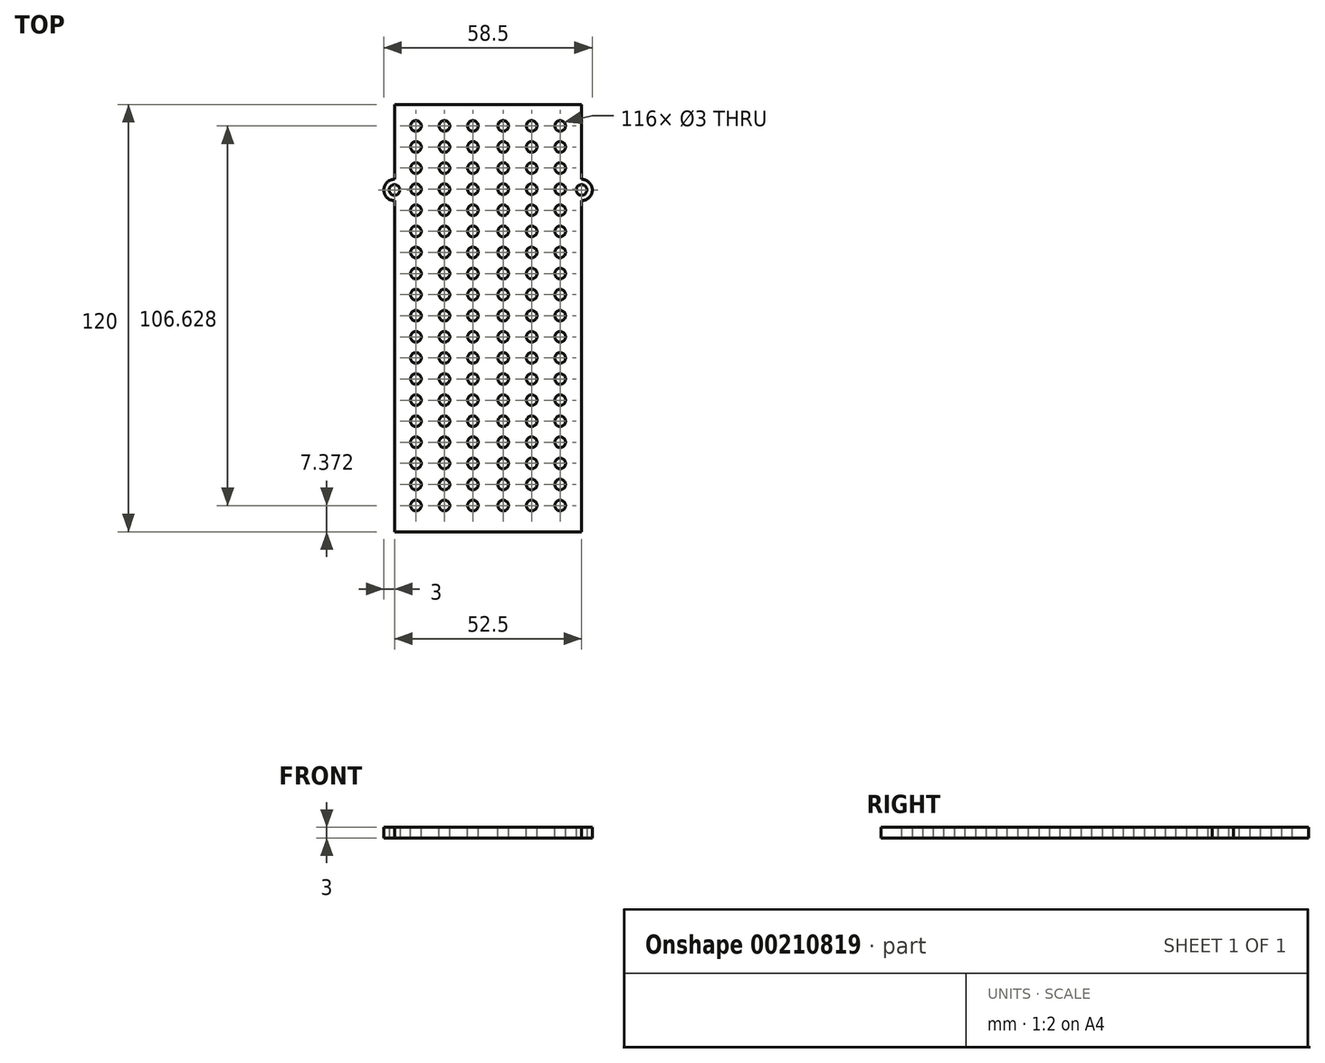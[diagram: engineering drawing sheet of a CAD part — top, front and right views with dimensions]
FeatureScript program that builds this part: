
annotation { "Feature Type Name" : "Feature", "Feature Type Description" : "" }
export const myFeature = defineFeature(function(context is Context, id is Id, definition is map)
    precondition{}
    {
        {
            var Q0;
            Q0=qCreatedBy(makeId("Top.planeOp"),FACE);
            var sketch = newSketch(context, id + "F0", { "sketchPlane" : qUnion([Q0])});
            skCircle(sketch, "E0", {"center": v(-26.25, 36) * mm, "radius": 1.5 * mm});
            skCircle(sketch, "E1", {"center": v(26.25, 36) * mm, "radius": 1.5 * mm});
            skLineSegment(sketch, "E2.bottom", {"start": v(-26.25, 60) * mm, "end": v(26.25, 60) * mm});
            skLineSegment(sketch, "E2.top", {"start": v(-26.25, -60) * mm, "end": v(26.25, -60) * mm});
            skLineSegment(sketch, "E2.left", {"start": v(-26.25, 60) * mm, "end": v(-26.25, 39) * mm});
            skPoint(sketch, "E2.middle", {"position": v(0, 0) * mm});
            skLineSegment(sketch, "E3", {"start": v(26.25, -60) * mm, "end": v(26.25, 33) * mm});
            skArc(sketch, "E4", {"start": v(-26.25, 39) * mm, "mid": v(-29.25, 36) * mm, "end": v(-26.25, 33) * mm});
            skArc(sketch, "E5", {"start": v(26.25, 33) * mm, "mid": v(29.25, 36) * mm, "end": v(26.25, 39) * mm});
            skLineSegment(sketch, "E6.trimOffspring", {"start": v(-26.25, 33) * mm, "end": v(-26.25, -60) * mm});
            skLineSegment(sketch, "E7.trimOffspring", {"start": v(26.25, 39) * mm, "end": v(26.25, 60) * mm});
            skSolve(sketch);
        }
        {
            var Q0;
            Q0 = qSketchRegion(id + "F0", true);
            extrude(context, id + "F1", {"entities" : qUnion([Q0]), "depth" : 3 * mm});
        }
        {
            var Q0;
            Q0=makeQuery(id+"F1.opExtrude","CAP_FACE",FACE,{"disambiguationData":[OSD([sQuery(id+"F0.wireOp",EDGE,"E0"),sQuery(id+"F0.wireOp",EDGE,"E1"),sQuery(id+"F0.wireOp",EDGE,"E2.bottom"),sQuery(id+"F0.wireOp",EDGE,"E2.top"),sQuery(id+"F0.wireOp",EDGE,"E2.left"),sQuery(id+"F0.wireOp",EDGE,"E3"),sQuery(id+"F0.wireOp",EDGE,"E4"),sQuery(id+"F0.wireOp",EDGE,"E5"),sQuery(id+"F0.wireOp",EDGE,"E6.trimOffspring"),sQuery(id+"F0.wireOp",EDGE,"E7.trimOffspring")])],"isStart":false});
            var sketch = newSketch(context, id + "F2", { "sketchPlane" : qUnion([Q0])});
            skLineSegment(sketch, "E8", {"start": v(-26.25, 54) * mm, "end": v(26.25, 54) * mm, "construction": true});
            skCircle(sketch, "E9", {"center": v(-20.25, 54) * mm, "radius": 1.5 * mm});
            skCircle(sketch, "E10", {"center": v(20.25, 54) * mm, "radius": 1.5 * mm});
            skCircle(sketch, "E11", {"center": v(-12.25, 54) * mm, "radius": 1.5 * mm});
            skCircle(sketch, "E12", {"center": v(12.25, 54) * mm, "radius": 1.5 * mm});
            skCircle(sketch, "E13", {"center": v(-4.25, 54) * mm, "radius": 1.5 * mm});
            skCircle(sketch, "E14", {"center": v(4.25, 54) * mm, "radius": 1.5 * mm});
            skLineSegment(sketch, "E15.direction1", {"start": v(-20.25, 54) * mm, "end": v(-20.25, 48.08) * mm, "construction": true});
            skCircle(sketch, "E16.0.1.0", {"center": v(-20.25, 48.08) * mm, "radius": 1.5 * mm});
            skCircle(sketch, "E16.2.1.0", {"center": v(-12.25, 48.08) * mm, "radius": 1.5 * mm});
            skCircle(sketch, "E16.4.1.0", {"center": v(-4.25, 48.08) * mm, "radius": 1.5 * mm});
            skCircle(sketch, "E16.6.1.0", {"center": v(4.25, 48.08) * mm, "radius": 1.5 * mm});
            skCircle(sketch, "E16.8.1.0", {"center": v(12.25, 48.08) * mm, "radius": 1.5 * mm});
            skCircle(sketch, "E16.10.1.0", {"center": v(20.25, 48.08) * mm, "radius": 1.5 * mm});
            skCircle(sketch, "E16.0.2.0", {"center": v(-20.25, 42.15) * mm, "radius": 1.5 * mm});
            skCircle(sketch, "E16.2.2.0", {"center": v(-12.25, 42.15) * mm, "radius": 1.5 * mm});
            skCircle(sketch, "E16.4.2.0", {"center": v(-4.25, 42.15) * mm, "radius": 1.5 * mm});
            skCircle(sketch, "E16.6.2.0", {"center": v(4.25, 42.15) * mm, "radius": 1.5 * mm});
            skCircle(sketch, "E16.8.2.0", {"center": v(12.25, 42.15) * mm, "radius": 1.5 * mm});
            skCircle(sketch, "E16.10.2.0", {"center": v(20.25, 42.15) * mm, "radius": 1.5 * mm});
            skCircle(sketch, "E16.0.3.0", {"center": v(-20.25, 36.23) * mm, "radius": 1.5 * mm});
            skCircle(sketch, "E16.2.3.0", {"center": v(-12.25, 36.23) * mm, "radius": 1.5 * mm});
            skCircle(sketch, "E16.4.3.0", {"center": v(-4.25, 36.23) * mm, "radius": 1.5 * mm});
            skCircle(sketch, "E16.6.3.0", {"center": v(4.25, 36.23) * mm, "radius": 1.5 * mm});
            skCircle(sketch, "E16.8.3.0", {"center": v(12.25, 36.23) * mm, "radius": 1.5 * mm});
            skCircle(sketch, "E16.10.3.0", {"center": v(20.25, 36.23) * mm, "radius": 1.5 * mm});
            skCircle(sketch, "E16.0.4.0", {"center": v(-20.25, 30.3) * mm, "radius": 1.5 * mm});
            skCircle(sketch, "E16.2.4.0", {"center": v(-12.25, 30.3) * mm, "radius": 1.5 * mm});
            skCircle(sketch, "E16.4.4.0", {"center": v(-4.25, 30.3) * mm, "radius": 1.5 * mm});
            skCircle(sketch, "E16.6.4.0", {"center": v(4.25, 30.3) * mm, "radius": 1.5 * mm});
            skCircle(sketch, "E16.8.4.0", {"center": v(12.25, 30.3) * mm, "radius": 1.5 * mm});
            skCircle(sketch, "E16.10.4.0", {"center": v(20.25, 30.3) * mm, "radius": 1.5 * mm});
            skCircle(sketch, "E16.0.5.0", {"center": v(-20.25, 24.38) * mm, "radius": 1.5 * mm});
            skCircle(sketch, "E16.2.5.0", {"center": v(-12.25, 24.38) * mm, "radius": 1.5 * mm});
            skCircle(sketch, "E16.4.5.0", {"center": v(-4.25, 24.38) * mm, "radius": 1.5 * mm});
            skCircle(sketch, "E16.6.5.0", {"center": v(4.25, 24.38) * mm, "radius": 1.5 * mm});
            skCircle(sketch, "E16.8.5.0", {"center": v(12.25, 24.38) * mm, "radius": 1.5 * mm});
            skCircle(sketch, "E16.10.5.0", {"center": v(20.25, 24.38) * mm, "radius": 1.5 * mm});
            skCircle(sketch, "E16.0.6.0", {"center": v(-20.25, 18.46) * mm, "radius": 1.5 * mm});
            skCircle(sketch, "E16.2.6.0", {"center": v(-12.25, 18.46) * mm, "radius": 1.5 * mm});
            skCircle(sketch, "E16.4.6.0", {"center": v(-4.25, 18.46) * mm, "radius": 1.5 * mm});
            skCircle(sketch, "E16.6.6.0", {"center": v(4.25, 18.46) * mm, "radius": 1.5 * mm});
            skCircle(sketch, "E16.8.6.0", {"center": v(12.25, 18.46) * mm, "radius": 1.5 * mm});
            skCircle(sketch, "E16.10.6.0", {"center": v(20.25, 18.46) * mm, "radius": 1.5 * mm});
            skCircle(sketch, "E16.0.7.0", {"center": v(-20.25, 12.53) * mm, "radius": 1.5 * mm});
            skCircle(sketch, "E16.2.7.0", {"center": v(-12.25, 12.53) * mm, "radius": 1.5 * mm});
            skCircle(sketch, "E16.4.7.0", {"center": v(-4.25, 12.53) * mm, "radius": 1.5 * mm});
            skCircle(sketch, "E16.6.7.0", {"center": v(4.25, 12.53) * mm, "radius": 1.5 * mm});
            skCircle(sketch, "E16.8.7.0", {"center": v(12.25, 12.53) * mm, "radius": 1.5 * mm});
            skCircle(sketch, "E16.10.7.0", {"center": v(20.25, 12.53) * mm, "radius": 1.5 * mm});
            skCircle(sketch, "E16.0.8.0", {"center": v(-20.25, 6.6) * mm, "radius": 1.5 * mm});
            skCircle(sketch, "E16.2.8.0", {"center": v(-12.25, 6.6) * mm, "radius": 1.5 * mm});
            skCircle(sketch, "E16.4.8.0", {"center": v(-4.25, 6.6) * mm, "radius": 1.5 * mm});
            skCircle(sketch, "E16.6.8.0", {"center": v(4.25, 6.6) * mm, "radius": 1.5 * mm});
            skCircle(sketch, "E16.8.8.0", {"center": v(12.25, 6.6) * mm, "radius": 1.5 * mm});
            skCircle(sketch, "E16.10.8.0", {"center": v(20.25, 6.6) * mm, "radius": 1.5 * mm});
            skCircle(sketch, "E16.0.9.0", {"center": v(-20.25, 0.69) * mm, "radius": 1.5 * mm});
            skCircle(sketch, "E16.2.9.0", {"center": v(-12.25, 0.69) * mm, "radius": 1.5 * mm});
            skCircle(sketch, "E16.4.9.0", {"center": v(-4.25, 0.69) * mm, "radius": 1.5 * mm});
            skCircle(sketch, "E16.6.9.0", {"center": v(4.25, 0.69) * mm, "radius": 1.5 * mm});
            skCircle(sketch, "E16.8.9.0", {"center": v(12.25, 0.69) * mm, "radius": 1.5 * mm});
            skCircle(sketch, "E16.10.9.0", {"center": v(20.25, 0.69) * mm, "radius": 1.5 * mm});
            skCircle(sketch, "E17.0.10.0", {"center": v(-20.25, -5.24) * mm, "radius": 1.5 * mm});
            skCircle(sketch, "E17.2.10.0", {"center": v(-12.25, -5.24) * mm, "radius": 1.5 * mm});
            skCircle(sketch, "E17.4.10.0", {"center": v(-4.25, -5.24) * mm, "radius": 1.5 * mm});
            skCircle(sketch, "E17.6.10.0", {"center": v(4.25, -5.24) * mm, "radius": 1.5 * mm});
            skCircle(sketch, "E17.8.10.0", {"center": v(12.25, -5.24) * mm, "radius": 1.5 * mm});
            skCircle(sketch, "E17.10.10.0", {"center": v(20.25, -5.24) * mm, "radius": 1.5 * mm});
            skCircle(sketch, "E17.0.11.0", {"center": v(-20.25, -11.16) * mm, "radius": 1.5 * mm});
            skCircle(sketch, "E17.2.11.0", {"center": v(-12.25, -11.16) * mm, "radius": 1.5 * mm});
            skCircle(sketch, "E17.4.11.0", {"center": v(-4.25, -11.16) * mm, "radius": 1.5 * mm});
            skCircle(sketch, "E17.6.11.0", {"center": v(4.25, -11.16) * mm, "radius": 1.5 * mm});
            skCircle(sketch, "E17.8.11.0", {"center": v(12.25, -11.16) * mm, "radius": 1.5 * mm});
            skCircle(sketch, "E17.10.11.0", {"center": v(20.25, -11.16) * mm, "radius": 1.5 * mm});
            skCircle(sketch, "E17.0.12.0", {"center": v(-20.25, -17.09) * mm, "radius": 1.5 * mm});
            skCircle(sketch, "E17.2.12.0", {"center": v(-12.25, -17.09) * mm, "radius": 1.5 * mm});
            skCircle(sketch, "E17.4.12.0", {"center": v(-4.25, -17.09) * mm, "radius": 1.5 * mm});
            skCircle(sketch, "E17.6.12.0", {"center": v(4.25, -17.09) * mm, "radius": 1.5 * mm});
            skCircle(sketch, "E17.8.12.0", {"center": v(12.25, -17.09) * mm, "radius": 1.5 * mm});
            skCircle(sketch, "E17.10.12.0", {"center": v(20.25, -17.09) * mm, "radius": 1.5 * mm});
            skCircle(sketch, "E17.0.13.0", {"center": v(-20.25, -23) * mm, "radius": 1.5 * mm});
            skCircle(sketch, "E17.2.13.0", {"center": v(-12.25, -23) * mm, "radius": 1.5 * mm});
            skCircle(sketch, "E17.4.13.0", {"center": v(-4.25, -23) * mm, "radius": 1.5 * mm});
            skCircle(sketch, "E17.6.13.0", {"center": v(4.25, -23) * mm, "radius": 1.5 * mm});
            skCircle(sketch, "E17.8.13.0", {"center": v(12.25, -23) * mm, "radius": 1.5 * mm});
            skCircle(sketch, "E17.10.13.0", {"center": v(20.25, -23) * mm, "radius": 1.5 * mm});
            skCircle(sketch, "E17.0.14.0", {"center": v(-20.25, -28.93) * mm, "radius": 1.5 * mm});
            skCircle(sketch, "E17.2.14.0", {"center": v(-12.25, -28.93) * mm, "radius": 1.5 * mm});
            skCircle(sketch, "E17.4.14.0", {"center": v(-4.25, -28.93) * mm, "radius": 1.5 * mm});
            skCircle(sketch, "E17.6.14.0", {"center": v(4.25, -28.93) * mm, "radius": 1.5 * mm});
            skCircle(sketch, "E17.8.14.0", {"center": v(12.25, -28.93) * mm, "radius": 1.5 * mm});
            skCircle(sketch, "E17.10.14.0", {"center": v(20.25, -28.93) * mm, "radius": 1.5 * mm});
            skCircle(sketch, "E17.0.15.0", {"center": v(-20.25, -34.86) * mm, "radius": 1.5 * mm});
            skCircle(sketch, "E17.2.15.0", {"center": v(-12.25, -34.86) * mm, "radius": 1.5 * mm});
            skCircle(sketch, "E17.4.15.0", {"center": v(-4.25, -34.86) * mm, "radius": 1.5 * mm});
            skCircle(sketch, "E17.6.15.0", {"center": v(4.25, -34.86) * mm, "radius": 1.5 * mm});
            skCircle(sketch, "E17.8.15.0", {"center": v(12.25, -34.86) * mm, "radius": 1.5 * mm});
            skCircle(sketch, "E17.10.15.0", {"center": v(20.25, -34.86) * mm, "radius": 1.5 * mm});
            skCircle(sketch, "E17.0.16.0", {"center": v(-20.25, -40.78) * mm, "radius": 1.5 * mm});
            skCircle(sketch, "E17.2.16.0", {"center": v(-12.25, -40.78) * mm, "radius": 1.5 * mm});
            skCircle(sketch, "E17.4.16.0", {"center": v(-4.25, -40.78) * mm, "radius": 1.5 * mm});
            skCircle(sketch, "E17.6.16.0", {"center": v(4.25, -40.78) * mm, "radius": 1.5 * mm});
            skCircle(sketch, "E17.8.16.0", {"center": v(12.25, -40.78) * mm, "radius": 1.5 * mm});
            skCircle(sketch, "E17.10.16.0", {"center": v(20.25, -40.78) * mm, "radius": 1.5 * mm});
            skCircle(sketch, "E17.0.17.0", {"center": v(-20.25, -46.7) * mm, "radius": 1.5 * mm});
            skCircle(sketch, "E17.2.17.0", {"center": v(-12.25, -46.7) * mm, "radius": 1.5 * mm});
            skCircle(sketch, "E17.4.17.0", {"center": v(-4.25, -46.7) * mm, "radius": 1.5 * mm});
            skCircle(sketch, "E17.6.17.0", {"center": v(4.25, -46.7) * mm, "radius": 1.5 * mm});
            skCircle(sketch, "E17.8.17.0", {"center": v(12.25, -46.7) * mm, "radius": 1.5 * mm});
            skCircle(sketch, "E17.10.17.0", {"center": v(20.25, -46.7) * mm, "radius": 1.5 * mm});
            skCircle(sketch, "E17.0.18.0", {"center": v(-20.25, -52.63) * mm, "radius": 1.5 * mm});
            skCircle(sketch, "E17.2.18.0", {"center": v(-12.25, -52.63) * mm, "radius": 1.5 * mm});
            skCircle(sketch, "E17.4.18.0", {"center": v(-4.25, -52.63) * mm, "radius": 1.5 * mm});
            skCircle(sketch, "E17.6.18.0", {"center": v(4.25, -52.63) * mm, "radius": 1.5 * mm});
            skCircle(sketch, "E17.8.18.0", {"center": v(12.25, -52.63) * mm, "radius": 1.5 * mm});
            skCircle(sketch, "E17.10.18.0", {"center": v(20.25, -52.63) * mm, "radius": 1.5 * mm});
            skSolve(sketch);
        }
        {
            var Q0;
            Q0 = qSketchRegion(id + "F2", true);
            extrude(context, id + "F3", {"entities" : qUnion([Q0]), "operationType" : NewBodyOperationType.REMOVE, "oppositeDirection" : true, "depth" : 25 * mm});
        }
    });
